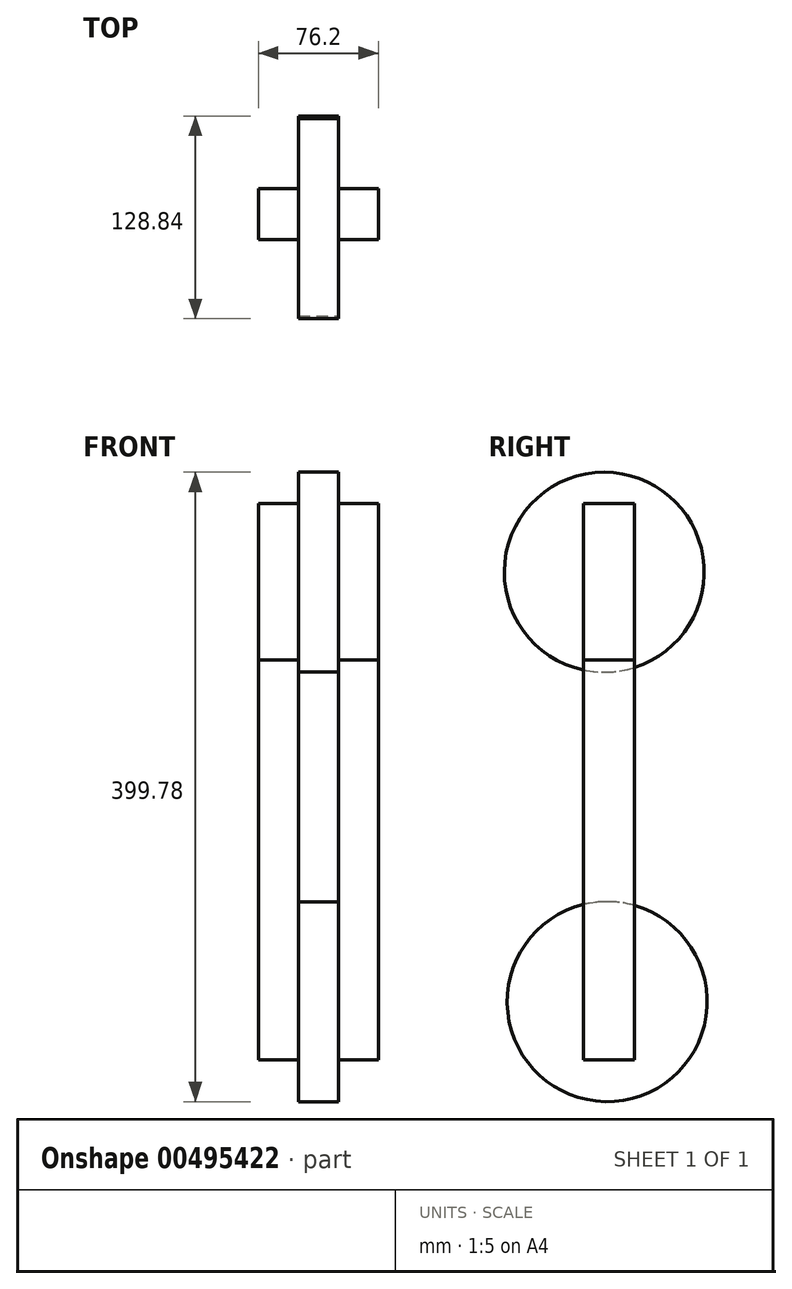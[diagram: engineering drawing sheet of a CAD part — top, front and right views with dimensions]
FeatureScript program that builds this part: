
annotation { "Feature Type Name" : "Feature", "Feature Type Description" : "" }
export const myFeature = defineFeature(function(context is Context, id is Id, definition is map)
    precondition{}
    {
        {
            var Q0;
            Q0=qCreatedBy(makeId("Front.planeOp"),FACE);
            var sketch = newSketch(context, id + "F0", { "sketchPlane" : qUnion([Q0])});
            skLineSegment(sketch, "E0.bottom", {"start": v(-38.1, 118.83) * mm, "end": v(-12.7, 118.83) * mm});
            skLineSegment(sketch, "E0.top", {"start": v(-38.1, -135.17) * mm, "end": v(-12.7, -135.17) * mm});
            skLineSegment(sketch, "E0.left", {"start": v(-38.1, 118.83) * mm, "end": v(-38.1, -135.17) * mm});
            skLineSegment(sketch, "E0.right", {"start": v(-12.7, 118.83) * mm, "end": v(-12.7, -135.17) * mm});
            skLineSegment(sketch, "E1", {"start": v(0, -46.52) * mm, "end": v(0, 74.65) * mm, "construction": true});
            skLineSegment(sketch, "E2.MirrorCS", {"start": v(38.1, 118.83) * mm, "end": v(12.7, 118.83) * mm});
            skLineSegment(sketch, "E3.MirrorCS", {"start": v(12.7, 118.83) * mm, "end": v(12.7, -135.17) * mm});
            skLineSegment(sketch, "E4.MirrorCS", {"start": v(38.1, 118.83) * mm, "end": v(38.1, -135.17) * mm});
            skLineSegment(sketch, "E5.MirrorCS", {"start": v(38.1, -135.17) * mm, "end": v(12.7, -135.17) * mm});
            skSolve(sketch);
        }
        {
            var Q0;
            Q0 = qSketchRegion(id + "F0", true);
            var sketch = newSketch(context, id + "F1", { "sketchPlane" : qUnion([Q0])});
            skSolve(sketch);
        }
        {
            var Q0;
            Q0 = qSketchRegion(id + "F1", true);
            var Q1;
            Q1=makeQuery(id+"F0.imprint","IMPRINT",FACE,{"disambiguationData":[TD([[makeQuery(id+"F0.imprint","IMPRINT",EDGE,{"derivedFrom":sQuery(id+"F0.wireOp",EDGE,"E0.bottom")}),-1.0]])]});
            var Q2;
            Q2=makeQuery(id+"F0.imprint","IMPRINT",FACE,{"disambiguationData":[TD([[makeQuery(id+"F0.imprint","IMPRINT",EDGE,{"derivedFrom":sQuery(id+"F0.wireOp",EDGE,"E2.MirrorCS")}),1.0]])]});
            extrude(context, id + "F2", {"entities" : qUnion([Q0, Q1, Q2]), "depth" : 32.3 * mm});
        }
        {
            var Q0;
            Q0=makeQuery(id+"F2.opExtrude","SWEPT_FACE",FACE,{"disambiguationData":[OSD([sQuery(id+"F0.wireOp",EDGE,"E2.MirrorCS")])]});
            var Q1;
            Q1=makeQuery(id+"F2.opExtrude","SWEPT_FACE",FACE,{"disambiguationData":[OSD([sQuery(id+"F0.wireOp",EDGE,"E0.bottom")])]});
            extrude(context, id + "F3", {"entities" : qUnion([Q0, Q1]), "depth" : 99.4 * mm});
        }
        {
            var Q0;
            Q0=makeQuery(id+"F3.opExtrude","SWEPT_FACE",FACE,{"disambiguationData":[OSD([sQuery(id+"F0.wireOp",EDGE,"E2.MirrorCS"),sQuery(id+"F0.wireOp",EDGE,"E3.MirrorCS")])]});
            var sketch = newSketch(context, id + "F4", { "sketchPlane" : qUnion([Q0])});
            skCircle(sketch, "E6", {"center": v(19.14, 174.72) * mm, "radius": 63.5 * mm});
            skCircle(sketch, "E7", {"center": v(17.3, -98.06) * mm, "radius": 63.5 * mm});
            skSolve(sketch);
        }
        {
            var Q0;
            Q0 = qSketchRegion(id + "F4", true);
            extrude(context, id + "F5", {"entities" : qUnion([Q0]), "depth" : 25.4 * mm});
        }
    });
